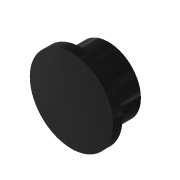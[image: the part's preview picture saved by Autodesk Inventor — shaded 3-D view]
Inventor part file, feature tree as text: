
AUTODESK INVENTOR PART (.ipt)
format: ipt  version: 2022.5 (Build 265521000, 521)  size: 90,624 bytes
history: native  units: mm
features: extrude x2, sketch x2
ambient origin geometry x8: Origin, YZ Plane, XZ Plane, XY Plane, X Axis, Y Axis, Z Axis, Center Point
bodies: Volumenkörper1 (feature_tree)
feature tree (4):
  extrude  "Extrusion1"  Depth=4.0mm TaperAngle=0.0deg
  extrude  "Extrusion2"  Depth=1.0mm TaperAngle=0.0deg
  sketch  "Skizze1"  dims[d0=7.0mm d1=4.0mm d2=0.0mm]
  sketch  "Skizze2"  dims[d3=9.0mm d4=1.0mm d5=0.0mm]
